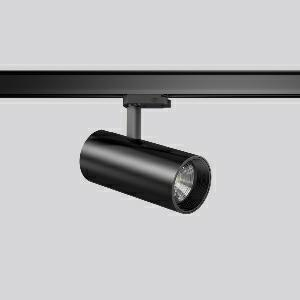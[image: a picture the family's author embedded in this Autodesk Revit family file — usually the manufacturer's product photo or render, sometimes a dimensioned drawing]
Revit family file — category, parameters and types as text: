
# Revit family: deecos_s_mini_742207_003_2_b607
name_source: partatom
category: Lighting Fixtures
units: mm (PartAtom-declared; Revit-internal decimal feet)

## family parameters
Cut with Voids When Loaded = No
Host = Face
Light Source = No
Part Type = Normal
Room Calculation Point = No
Round Connector Dimension = Use Diameter
Shared = No

## types (1)
- DEECOS S mini (1 x LED Modul 927, 2850 lm, 2700)
    Apparent Load = 29 VA
    Approval mark = CE
    CIE Flux Codes = 96 100 100 100 100
    Color Rendering = 92
    Color Temperature = 2700
    Default Elevation = 1800 mm
    Description = Series: DEECOS S mini
LED surface-mounted projector in modern design with no visible cooling ribs. Housing: die-cast aluminium, powder-coated. Rotation range: 356°. Swivel range: 90°. Black plastic ring and recessed LED to prevent glare from the side. Optical assembly with lens made of plastic (polycarbonate) for the best homogeneous light distribution - can be changed without tools. Best colour rendering index Ra>90. With multi adaptor for 3-circuit tracks 230 V. Suitable for Track on ceiling, Wall track. High quality converter without flickering and stroboscopic effect. The following accessories can be mounted without use of tools: interchangeable lenses, decorative glasses, honeycomb louvre, clear and frosted diffusers, white interchangeable plastic ring. 
Colour: deep black, matt (RAL 9005)
Diameter: 87 mm
Height: 214 mm
Lamp: LED
Socket: without socket
Colour temperature: 2700K
Colour rendering index (CRI): 92
System power: 29 W
Rated luminous flux: 2850 lm
Luminous efficiency: 98 lm/W
Control gear: Regulated power supply
Protection class: I
Type of protection: IP 20
    Height = 214 mm
    Lamp = 1 x LED Modul 927
    Lamp Light Flux = 2850 lm
    Lamp count = 1
    Length = 87 mm
    Lifetime = 50000 h
    Luminous efficacy = 98 lm/W
    Manufacturer = RZB
    ModVariant = No
    Model = 742207.003.2
    Mounting Place = Ceiling
    Mounting Type = Rail mounted
    Number of Poles = 1
    OnlyDefault = Yes
    Power Factor = 1
    Product Name = DEECOS S mini
    Product group = Track mounted projectors
    ProductGroupID = 301
    Protection Class = Protection class I
    Protection Degree = IP 20
    RLX_Detail_Level = 1
    RLX_Emergency_Light_Flux = 0 lm
    RLX_Emergency_Type = 0
    RLX_Emergency_Type_DB = No
    RlxData = <blob elided: 38857 chars, md5=0fc97962>
    Socket = socket
    Standby Power = 0 W
    System Light Flux = 2850 lm
    System Power = 29 W
    Type Comments = Product without accessories
    Type Image = 741930.003.jpg
    URL = http://relux.com
    VarID = ---
    Voltage = 230 V
    Voltage Range = 220-240 V
    Weight = 0.00 kg
    Width = 0 mm  [stored 0 ft]

note: [stored X ft] marks values corroborated as IEEE doubles in the binary element streams (Revit-internal decimal feet)

## geometry (parser evidence)
native form markers: Blend x4, Sweep x12
no freeform markers — native parametric forms only
